# Revit family: Sink-Wading_Pool-Kohler-2833
name_source: partatom
category: Plumbing Fixtures
revit_build: Autodesk Revit MEP 2012 (Build: 20110916_2132(x64)
units: mm (PartAtom-declared; Revit-internal decimal feet)

## types (17) — shared parameters
Date Modified = January 26, 2015
Default Elevation = 48 "
Depth = 15.625 "
Equipment Abbreviation = WS
Family Version = 1.0
Height = 7 "
Manufacturer = Kohler Company
Model Disclaimer = Contact Kohler Company For More Information
Product Page URL = http://www.us.kohler.com
URL = http://www.us.kohler.com
Width = 18.25 "
zz Length 1 = 7 "
zz Length 2 = 0.75 "
zz Length 3 = 15.625 "
zz Length 4 = 18.25 "

## per-type parameters (varying)
| type | Description | Model | Product Material | zz Integer 1 |
| White | DemiLav Wading Pool Bathroom Sink, White | K-2833-0 | Vitreous China - Kohler - White | 1 |
| Sea Salt | DemiLav Wading Pool Bathroom Sink, Sea Salt | K-2833-FF | Vitreous China - Kohler - Sea Salt | 2 |
| Biscuit | DemiLav Wading Pool Bathroom Sink, Biscuit | K-2833-96 | Vitreous China - Kohler - Biscuit | 3 |
| Almond | DemiLav Wading Pool Bathroom Sink, Almond | K-2833-47 | Vitreous China - Kohler - Almond | 4 |
| Cane Sugar | DemiLav Wading Pool Bathroom Sink, Cane Sugar | K-2833-FD | Vitreous China - Kohler - Cane Sugar | 5 |
| Dune | DemiLav Wading Pool Bathroom Sink, Dune | K-2833-NY | Vitreous China - Kohler - Dune | 6 |
| Ice Grey | DemiLav Wading Pool Bathroom Sink, Ice Grey | K-2833-95 | Vitreous China - Kohler - Ice Grey | 7 |
| Sandbar | DemiLav Wading Pool Bathroom Sink, Sandbar | K-2833-G9 | Vitreous China - Kohler - Sandbar | 8 |
| Mexican Sand | DemiLav Wading Pool Bathroom Sink, Mexican Sand | K-2833-33 | Vitreous China - Kohler - Mexican Sand | 9 |
| Vapour Blue | DemiLav Wading Pool Bathroom Sink, Vapour Blue | K-2833-KC | Vitreous China - Kohler - Vapour Blue | 10 |
| Vapour Green | DemiLav Wading Pool Bathroom Sink, Vapour Green | K-2833-KG | Vitreous China - Kohler - Vapour Green | 11 |
| Cashmere | DemiLav Wading Pool Bathroom Sink, Cashmere | K-2833-K4 | Vitreous China - Kohler - Cashmere | 12 |
| Basalt | DemiLav Wading Pool Bathroom Sink, Basalt | K-2833-FT | Vitreous China - Kohler - Basalt | 13 |
| Thunder Grey | DemiLav Wading Pool Bathroom Sink, Thunder Grey | K-2833-58 | Vitreous China - Kohler - Thunder Grey | 14 |
| Suede | DemiLav Wading Pool Bathroom Sink, Suede | K-2833-20 | Vitreous China - Kohler - Suede | 15 |
| Black n Tan | DemiLav Wading Pool Bathroom Sink, Black 'n Tan | K-2833-KA | Vitreous China - Kohler - Black n Tan | 16 |
| Black | DemiLav Wading Pool Bathroom Sink, Black | K-2833-7 | Vitreous China - Kohler - Black | 17 |

## geometry (parser evidence)
native form markers: Blend x20, Sweep x2
no freeform markers — native parametric forms only
